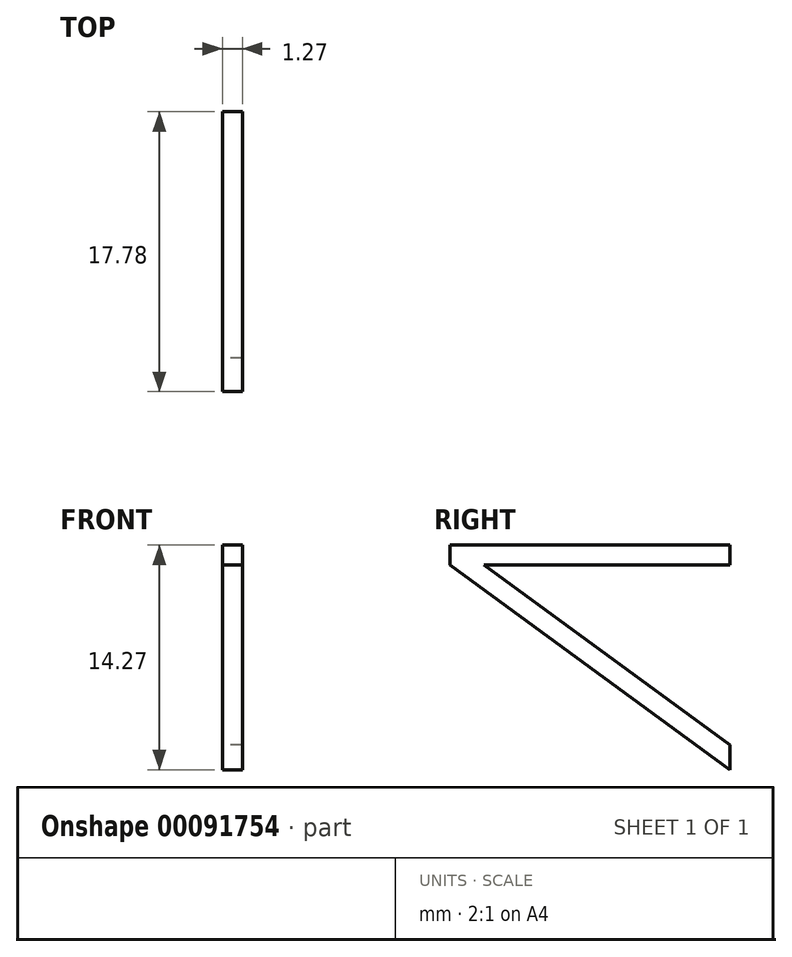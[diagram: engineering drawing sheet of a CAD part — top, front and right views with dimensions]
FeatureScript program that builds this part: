
annotation { "Feature Type Name" : "Feature", "Feature Type Description" : "" }
export const myFeature = defineFeature(function(context is Context, id is Id, definition is map)
    precondition{}
    {
        {
            var Q0;
            Q0=qCreatedBy(makeId("Right.planeOp"),FACE);
            var sketch = newSketch(context, id + "F0", { "sketchPlane" : qUnion([Q0])});
            skLineSegment(sketch, "E0.bottom", {"start": v(1.84, -8.34) * mm, "end": v(19.62, -8.34) * mm});
            skLineSegment(sketch, "E0.top", {"start": v(4, -9.61) * mm, "end": v(19.62, -9.61) * mm});
            skLineSegment(sketch, "E0.left", {"start": v(1.84, -8.34) * mm, "end": v(1.84, -9.61) * mm});
            skLineSegment(sketch, "E0.right", {"start": v(19.62, -8.34) * mm, "end": v(19.62, -9.61) * mm});
            skLineSegment(sketch, "E1", {"start": v(1.84, -9.61) * mm, "end": v(19.62, -22.61) * mm});
            skLineSegment(sketch, "E2", {"start": v(19.62, -22.61) * mm, "end": v(19.62, -21.04) * mm});
            skLineSegment(sketch, "E3", {"start": v(19.62, -21.04) * mm, "end": v(4, -9.61) * mm});
            skSolve(sketch);
        }
        {
            var Q0;
            Q0 = qSketchRegion(id + "F0", true);
            extrude(context, id + "F1", {"entities" : qUnion([Q0]), "depth" : 1.27 * mm});
        }
    });
